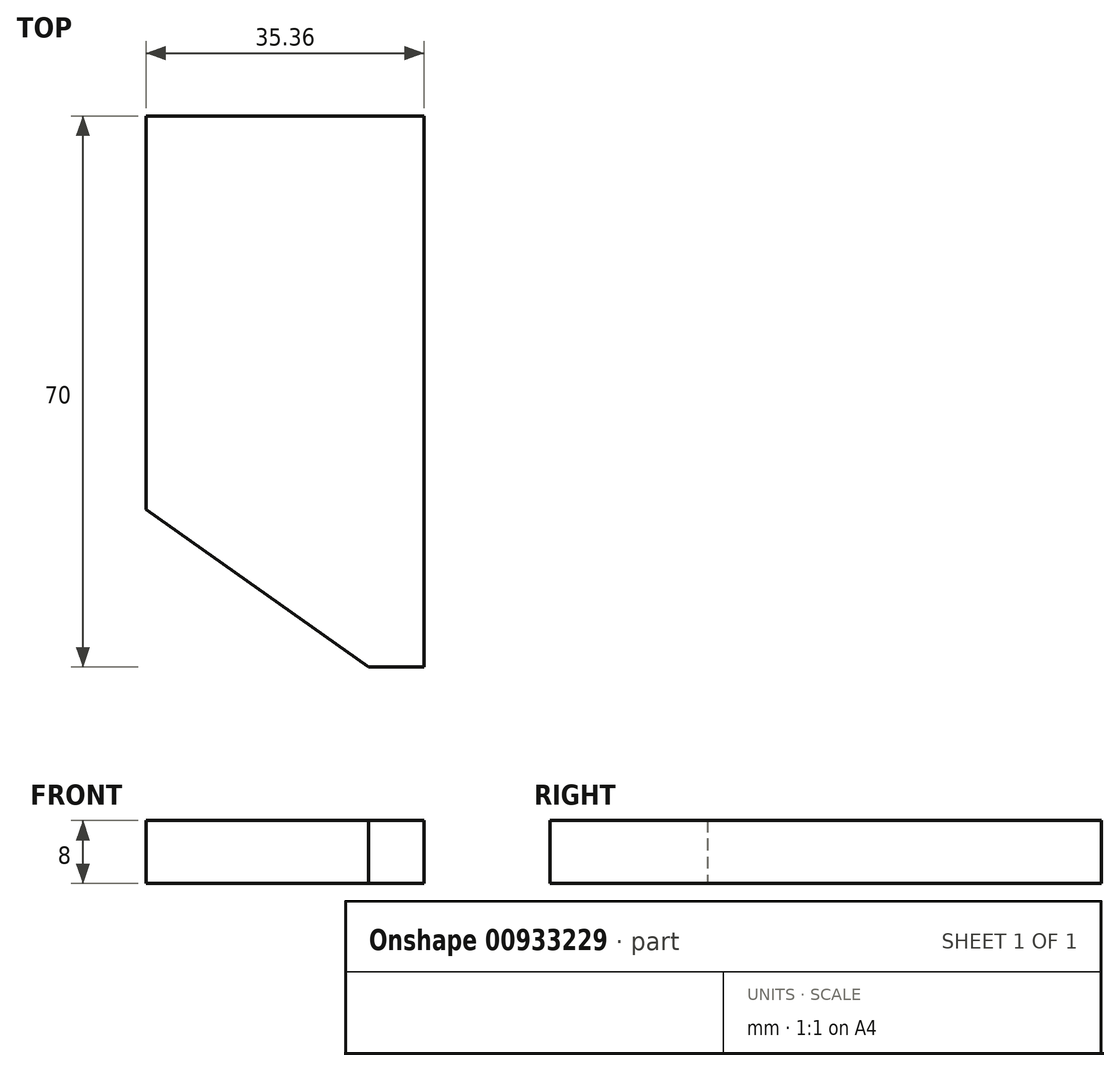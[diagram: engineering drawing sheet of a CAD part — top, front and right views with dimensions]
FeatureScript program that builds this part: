
annotation { "Feature Type Name" : "Feature", "Feature Type Description" : "" }
export const myFeature = defineFeature(function(context is Context, id is Id, definition is map)
    precondition{}
    {
        {
            var Q0;
            Q0=qCreatedBy(makeId("Top.planeOp"),FACE);
            var sketch = newSketch(context, id + "F0", { "sketchPlane" : qUnion([Q0])});
            skLineSegment(sketch, "E0", {"start": v(35.36, 50) * mm, "end": v(35.36, -20) * mm});
            skLineSegment(sketch, "E1", {"start": v(35.36, -20) * mm, "end": v(28.28, -20) * mm});
            skLineSegment(sketch, "E2", {"start": v(28.28, -20) * mm, "end": v(0, 0) * mm});
            skLineSegment(sketch, "E3", {"start": v(0, 0) * mm, "end": v(0, 50) * mm});
            skLineSegment(sketch, "E4", {"start": v(0, 50) * mm, "end": v(35.36, 50) * mm});
            skSolve(sketch);
        }
        {
            var Q0;
            Q0 = qSketchRegion(id + "F0", true);
            extrude(context, id + "F1", {"entities" : qUnion([Q0]), "depth" : 8 * mm, "offsetDistance" : 25 * mm});
        }
    });
